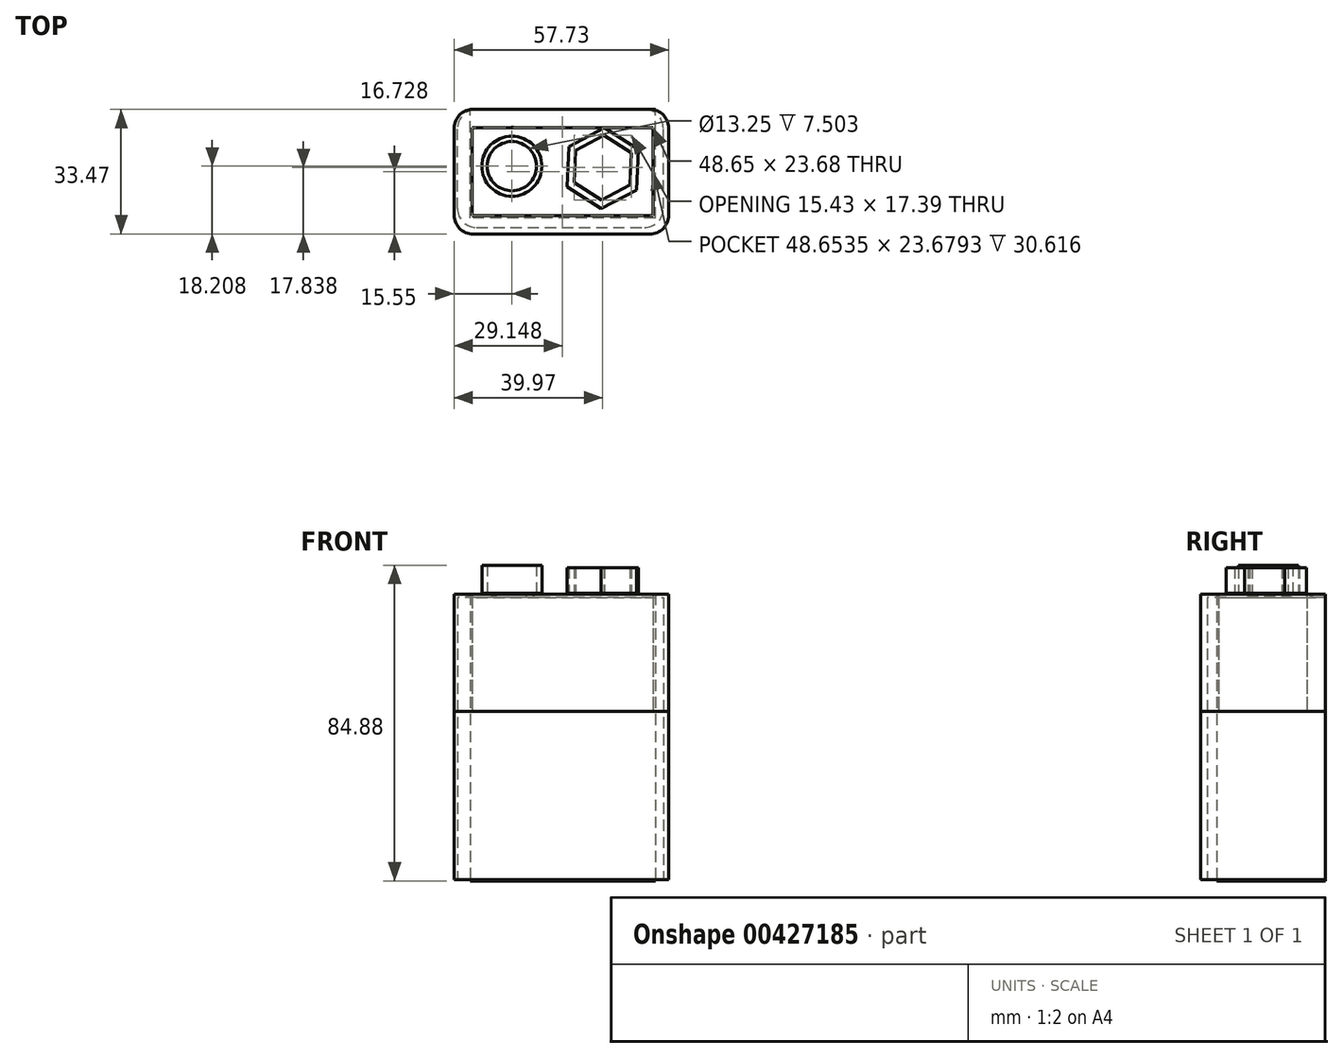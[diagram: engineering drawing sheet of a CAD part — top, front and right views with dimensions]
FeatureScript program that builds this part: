
annotation { "Feature Type Name" : "Feature", "Feature Type Description" : "" }
export const myFeature = defineFeature(function(context is Context, id is Id, definition is map)
    precondition{}
    {
        {
            var Q0;
            Q0=qCreatedBy(makeId("Front.planeOp"),FACE);
            var sketch = newSketch(context, id + "F0", { "sketchPlane" : qUnion([Q0])});
            skLineSegment(sketch, "E0.bottom", {"start": v(-26.82, 30.62) * mm, "end": v(28.49, 30.62) * mm});
            skLineSegment(sketch, "E0.top", {"start": v(-26.82, -45.23) * mm, "end": v(28.49, -45.23) * mm});
            skLineSegment(sketch, "E0.left", {"start": v(-26.82, 30.62) * mm, "end": v(-26.82, -45.23) * mm});
            skLineSegment(sketch, "E0.right", {"start": v(28.49, 30.62) * mm, "end": v(28.49, -45.23) * mm});
            skSolve(sketch);
        }
        {
            var Q0;
            Q0 = qSketchRegion(id + "F0", true);
            extrude(context, id + "F1", {"entities" : qUnion([Q0]), "depth" : 31.75 * mm});
        }
        {
            var Q0;
            Q0=makeQuery(id+"F1.opExtrude","CAP_EDGE",EDGE,{"disambiguationData":[OSD([sQuery(id+"F0.wireOp",EDGE,"E0.right")])],"isStart":false});
            var Q1;
            Q1=makeQuery(id+"F1.opExtrude","CAP_EDGE",EDGE,{"disambiguationData":[OSD([sQuery(id+"F0.wireOp",EDGE,"E0.left")])],"isStart":false});
            var Q2;
            Q2=makeQuery(id+"F1.opExtrude","CAP_EDGE",EDGE,{"disambiguationData":[OSD([sQuery(id+"F0.wireOp",EDGE,"E0.right")])],"isStart":true});
            var Q3;
            Q3=makeQuery(id+"F1.opExtrude","CAP_EDGE",EDGE,{"disambiguationData":[OSD([sQuery(id+"F0.wireOp",EDGE,"E0.left")])],"isStart":true});
            fillet(context, id + "F2", {"entities" : qUnion([Q0, Q1, Q2, Q3]), "radius" : 5.08 * mm, "tangentPropagation" : true, "allowEdgeOverflow" : false});
        }
        {
            var Q0;
            Q0=makeQuery(id+"F1.opExtrude","SWEPT_FACE",FACE,{"disambiguationData":[OSD([sQuery(id+"F0.wireOp",EDGE,"E0.bottom")])]});
            var sketch = newSketch(context, id + "F3", { "sketchPlane" : qUnion([Q0])});
            skCircle(sketch, "E1", {"center": v(-12.2, -15.26) * mm, "radius": 6.62 * mm});
            skCircle(sketch, "E2", {"center": v(-12.2, -15.26) * mm, "radius": 8.07 * mm});
            skSolve(sketch);
        }
        {
            var Q0;
            Q0=makeQuery(id+"F3.imprint","IMPRINT",FACE,{"disambiguationData":[TD([[makeQuery(id+"F3.imprint","IMPRINT",EDGE,{"derivedFrom":sQuery(id+"F3.wireOp",EDGE,"E1")}),-1.0]])]});
            var Q1;
            Q1=sQuery(id+"F3.wireOp",EDGE,"E2");
            var Q2;
            Q2=sQuery(id+"F3.wireOp",EDGE,"E1");
            extrude(context, id + "F4", {"entities" : qUnion([Q0]), "surfaceEntities" : qUnion([Q1, Q2]), "depth" : 8.64 * mm});
        }
        {
            var Q0;
            Q0=qCreatedBy(makeId("Top.planeOp"),FACE);
            var sketch = newSketch(context, id + "F5", { "sketchPlane" : qUnion([Q0])});
            skCircle(sketch, "E3", {"center": v(-12.02, -15.08) * mm, "radius": 10.21 * mm});
            skSolve(sketch);
        }
        {
            var Q0;
            Q0 = qSketchRegion(id + "F5", true);
            extrude(context, id + "F6", {"entities" : qUnion([Q0]), "operationType" : NewBodyOperationType.ADD, "depth" : 31.75 * mm});
        }
        {
            var Q0;
            Q0=makeQuery(id+"F6.boolean.opBoolean","INTERSECT",EDGE,{"derivedFrom":[makeQuery(id+"F1.opExtrude","SWEPT_FACE",FACE,{"disambiguationData":[OSD([sQuery(id+"F0.wireOp",EDGE,"E0.bottom")])]}),makeQuery(id+"F6.opExtrude","SWEPT_FACE",FACE,{"disambiguationData":[OSD([sQuery(id+"F5.wireOp",EDGE,"E3")])]})]});
            fillet(context, id + "F7", {"entities" : qUnion([Q0]), "radius" : 3.07 * mm, "tangentPropagation" : true, "allowEdgeOverflow" : false});
        }
        {
            var Q0;
            Q0=qCreatedBy(makeId("Top.planeOp"),FACE);
            var sketch = newSketch(context, id + "F8", { "sketchPlane" : qUnion([Q0])});
            skCircle(sketch, "E4.cCircle", {"center": v(12.2, -15.82) * mm, "radius": 10.84 * mm, "construction": true});
            skLineSegment(sketch, "E4.0", {"start": v(21.83, -10.82) * mm, "end": v(21.35, -21.65) * mm});
            skLineSegment(sketch, "E4.1", {"start": v(21.35, -21.65) * mm, "end": v(11.73, -26.65) * mm});
            skLineSegment(sketch, "E4.2", {"start": v(11.73, -26.65) * mm, "end": v(2.59, -20.81) * mm});
            skLineSegment(sketch, "E4.3", {"start": v(2.59, -20.81) * mm, "end": v(3.07, -9.98) * mm});
            skLineSegment(sketch, "E4.4", {"start": v(3.07, -9.98) * mm, "end": v(12.7, -4.99) * mm});
            skLineSegment(sketch, "E4.5", {"start": v(12.7, -4.99) * mm, "end": v(21.83, -10.82) * mm});
            skSolve(sketch);
        }
        {
            var Q0;
            Q0 = qSketchRegion(id + "F8", true);
            extrude(context, id + "F9", {"entities" : qUnion([Q0]), "operationType" : NewBodyOperationType.ADD, "depth" : 38.6 * mm});
        }
        {
            var Q0;
            Q0=qCreatedBy(makeId("Top.planeOp"),FACE);
            var sketch = newSketch(context, id + "F10", { "sketchPlane" : qUnion([Q0])});
            skCircle(sketch, "E5.cCircle", {"center": v(12.2, -15.63) * mm, "radius": 8.7 * mm, "construction": true});
            skLineSegment(sketch, "E5.0", {"start": v(12.58, -6.94) * mm, "end": v(19.92, -11.6) * mm});
            skLineSegment(sketch, "E5.1", {"start": v(19.92, -11.6) * mm, "end": v(19.55, -20.3) * mm});
            skLineSegment(sketch, "E5.2", {"start": v(19.55, -20.3) * mm, "end": v(11.84, -24.33) * mm});
            skLineSegment(sketch, "E5.3", {"start": v(11.84, -24.33) * mm, "end": v(4.5, -19.66) * mm});
            skLineSegment(sketch, "E5.4", {"start": v(4.5, -19.66) * mm, "end": v(4.86, -10.96) * mm});
            skLineSegment(sketch, "E5.5", {"start": v(4.86, -10.96) * mm, "end": v(12.58, -6.94) * mm});
            skSolve(sketch);
        }
        {
            var Q0;
            Q0 = qSketchRegion(id + "F10", true);
            extrude(context, id + "F11", {"entities" : qUnion([Q0]), "operationType" : NewBodyOperationType.REMOVE, "depth" : 38.86 * mm});
        }
        {
            var Q0;
            Q0=qCreatedBy(makeId("Top.planeOp"),FACE);
            var sketch = newSketch(context, id + "F12", { "sketchPlane" : qUnion([Q0])});
            skCircle(sketch, "E6.cCircle", {"center": v(12.4, -15.45) * mm, "radius": 8.27 * mm, "construction": true});
            skLineSegment(sketch, "E6.0", {"start": v(19.8, -11.75) * mm, "end": v(19.3, -20) * mm});
            skLineSegment(sketch, "E6.1", {"start": v(19.3, -20) * mm, "end": v(11.9, -23.7) * mm});
            skLineSegment(sketch, "E6.2", {"start": v(11.9, -23.7) * mm, "end": v(5, -19.15) * mm});
            skLineSegment(sketch, "E6.3", {"start": v(5, -19.15) * mm, "end": v(5.5, -10.89) * mm});
            skLineSegment(sketch, "E6.4", {"start": v(5.5, -10.89) * mm, "end": v(12.9, -7.19) * mm});
            skLineSegment(sketch, "E6.5", {"start": v(12.9, -7.19) * mm, "end": v(19.8, -11.75) * mm});
            skSolve(sketch);
        }
        {
            var Q0;
            Q0 = qSketchRegion(id + "F12", true);
            extrude(context, id + "F13", {"entities" : qUnion([Q0]), "operationType" : NewBodyOperationType.ADD, "depth" : 27.94 * mm});
        }
        {
            var Q0;
            Q0=qCreatedBy(makeId("Top.planeOp"),FACE);
            var sketch = newSketch(context, id + "F14", { "sketchPlane" : qUnion([Q0])});
            skLineSegment(sketch, "E7.bottom", {"start": v(-27.76, 0) * mm, "end": v(29.97, 0) * mm});
            skLineSegment(sketch, "E7.top", {"start": v(-27.76, -33.47) * mm, "end": v(29.97, -33.47) * mm});
            skLineSegment(sketch, "E7.left", {"start": v(-27.76, 0) * mm, "end": v(-27.76, -33.47) * mm});
            skLineSegment(sketch, "E7.right", {"start": v(29.97, 0) * mm, "end": v(29.97, -33.47) * mm});
            skSolve(sketch);
        }
        {
            var Q0;
            Q0 = qSketchRegion(id + "F14", true);
            extrude(context, id + "F15", {"entities" : qUnion([Q0]), "depth" : 31.5 * mm});
        }
        {
            var Q0;
            Q0 = qSketchRegion(id + "F14", true);
            extrude(context, id + "F16", {"entities" : qUnion([Q0]), "oppositeDirection" : true, "depth" : 45.2 * mm});
        }
        {
            var Q0;
            Q0=makeQuery(id+"F15.opExtrude","SWEPT_EDGE",EDGE,{"disambiguationData":[OSD([sQuery(id+"F14.wireOp",EDGE,"E7.top"),sQuery(id+"F14.wireOp",EDGE,"E7.right")])]});
            var Q1;
            Q1=makeQuery(id+"F16.opExtrude","SWEPT_EDGE",EDGE,{"disambiguationData":[OSD([sQuery(id+"F14.wireOp",EDGE,"E7.top"),sQuery(id+"F14.wireOp",EDGE,"E7.right")])]});
            var Q2;
            Q2=makeQuery(id+"F15.opExtrude","SWEPT_EDGE",EDGE,{"disambiguationData":[OSD([sQuery(id+"F14.wireOp",EDGE,"E7.top"),sQuery(id+"F14.wireOp",EDGE,"E7.left")])]});
            var Q3;
            Q3=makeQuery(id+"F16.opExtrude","SWEPT_EDGE",EDGE,{"disambiguationData":[OSD([sQuery(id+"F14.wireOp",EDGE,"E7.top"),sQuery(id+"F14.wireOp",EDGE,"E7.left")])]});
            var Q4;
            Q4=makeQuery(id+"F15.opExtrude","SWEPT_EDGE",EDGE,{"disambiguationData":[OSD([sQuery(id+"F14.wireOp",EDGE,"E7.bottom"),sQuery(id+"F14.wireOp",EDGE,"E7.left")])]});
            var Q5;
            Q5=makeQuery(id+"F16.opExtrude","SWEPT_EDGE",EDGE,{"disambiguationData":[OSD([sQuery(id+"F14.wireOp",EDGE,"E7.bottom"),sQuery(id+"F14.wireOp",EDGE,"E7.left")])]});
            var Q6;
            Q6=makeQuery(id+"F15.opExtrude","SWEPT_EDGE",EDGE,{"disambiguationData":[OSD([sQuery(id+"F14.wireOp",EDGE,"E7.bottom"),sQuery(id+"F14.wireOp",EDGE,"E7.right")])]});
            var Q7;
            Q7=makeQuery(id+"F16.opExtrude","SWEPT_EDGE",EDGE,{"disambiguationData":[OSD([sQuery(id+"F14.wireOp",EDGE,"E7.bottom"),sQuery(id+"F14.wireOp",EDGE,"E7.right")])]});
            fillet(context, id + "F17", {"entities" : qUnion([Q0, Q1, Q2, Q3, Q4, Q5, Q6, Q7]), "radius" : 5.08 * mm, "tangentPropagation" : true, "allowEdgeOverflow" : false});
        }
        {
            var Q0;
            Q0=qCreatedBy(makeId("Top.planeOp"),FACE);
            var sketch = newSketch(context, id + "F18", { "sketchPlane" : qUnion([Q0])});
            skLineSegment(sketch, "E8.bottom", {"start": v(-22.94, -4.9) * mm, "end": v(25.71, -4.9) * mm});
            skLineSegment(sketch, "E8.top", {"start": v(-22.94, -28.58) * mm, "end": v(25.71, -28.58) * mm});
            skLineSegment(sketch, "E8.left", {"start": v(-22.94, -4.9) * mm, "end": v(-22.94, -28.58) * mm});
            skLineSegment(sketch, "E8.right", {"start": v(25.71, -4.9) * mm, "end": v(25.71, -28.58) * mm});
            skSolve(sketch);
        }
        {
            var Q0;
            Q0 = qSketchRegion(id + "F18", true);
            extrude(context, id + "F19", {"entities" : qUnion([Q0]), "operationType" : NewBodyOperationType.REMOVE, "depth" : 31.75 * mm});
        }
        {
            var Q0;
            Q0=qCreatedBy(makeId("Front.planeOp"),FACE);
            var sketch = newSketch(context, id + "F20", { "sketchPlane" : qUnion([Q0])});
            skLineSegment(sketch, "E9.bottom", {"start": v(26.33, 31.46) * mm, "end": v(-23.45, 31.46) * mm});
            skLineSegment(sketch, "E9.top", {"start": v(26.33, -45.63) * mm, "end": v(-23.45, -45.63) * mm});
            skLineSegment(sketch, "E9.left", {"start": v(26.33, 31.46) * mm, "end": v(26.33, -45.63) * mm});
            skLineSegment(sketch, "E9.right", {"start": v(-23.45, 31.46) * mm, "end": v(-23.45, -45.63) * mm});
            skSolve(sketch);
        }
        {
            var Q0;
            Q0 = qSketchRegion(id + "F20", true);
            extrude(context, id + "F21", {"entities" : qUnion([Q0]), "depth" : 29.2 * mm});
        }
    });
